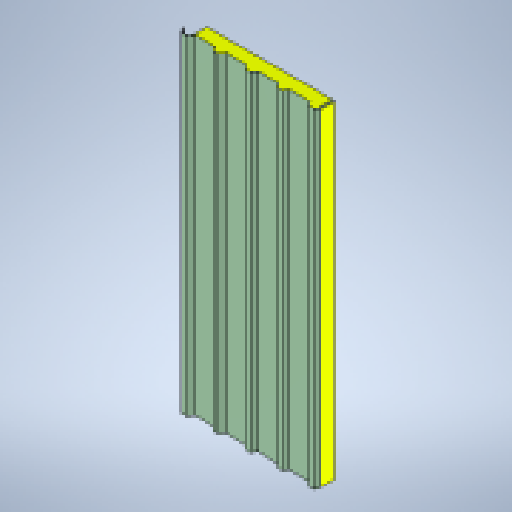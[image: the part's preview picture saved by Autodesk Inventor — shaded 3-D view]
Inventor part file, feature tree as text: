
AUTODESK INVENTOR PART (.ipt)
format: ipt  version: 2025 (Build 290162010, 162A)  size: 200,704 bytes
history: native  units: mm
features: extrude x2, sketch x2, chamfer x1, projected_geometry x1
ambient origin geometry x8: Origin, YZ Plane, XZ Plane, XY Plane, X Axis, Y Axis, Z Axis, Center Point
bodies: Solid1 (feature_tree)
feature tree (6):
  extrude  "Extrusion1"  Depth=2600.0mm
  extrude  "Extrusion2"  Depth=5.0mm
  chamfer  "Chamfer1"  Distance=40.0mm
  sketch  "Sketch2"  dims[d2=100.0mm d3=0.0mm d4=86.0mm d5=40.0mm d6=35.0mm d7=10.0mm d8=0.0mm d9=50.0mm d11=250.0mm d12=10.0mm d14=10.0mm d16=5.0mm d17=5.0mm d18=10.0mm d19=2.0mm d20=45.0deg]
  projected_geometry  "Projected Loop1"
  sketch  "Sketch Rectangular Pattern1"  dims[d0=1000.0mm d1=2600.0mm]
